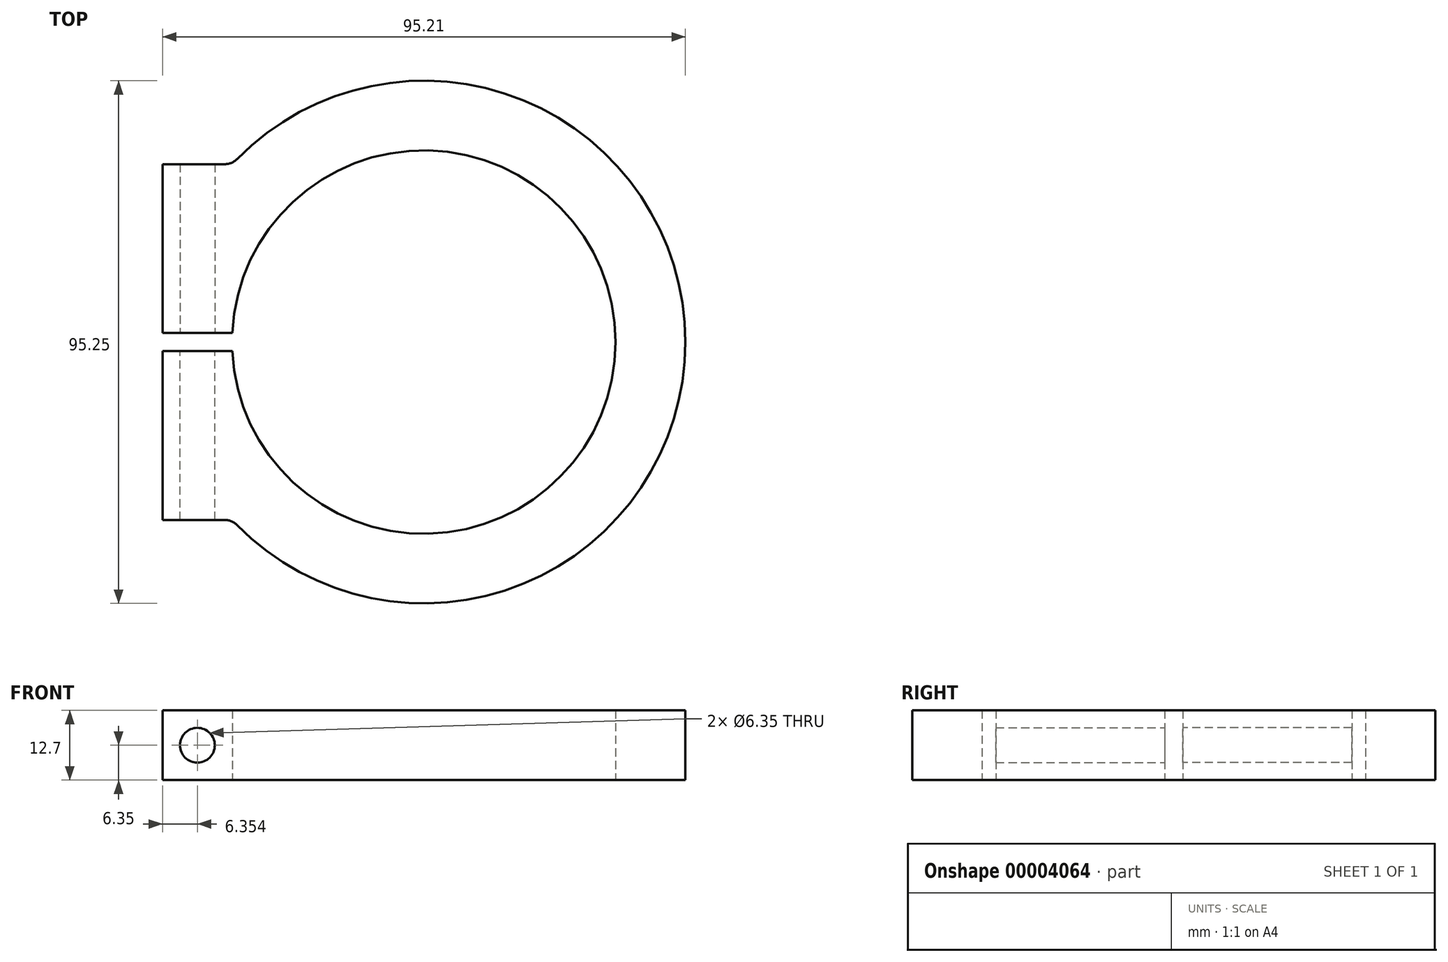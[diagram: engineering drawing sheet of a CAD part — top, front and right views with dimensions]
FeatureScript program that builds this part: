
annotation { "Feature Type Name" : "Feature", "Feature Type Description" : "" }
export const myFeature = defineFeature(function(context is Context, id is Id, definition is map)
    precondition{}
    {
        {
            var Q0;
            Q0=qCreatedBy(makeId("Top.planeOp"),FACE);
            var sketch = newSketch(context, id + "F0", { "sketchPlane" : qUnion([Q0])});
            skArc(sketch, "E0", {"start": v(0, 34.93) * mm, "mid": v(-24.1, 25.27) * mm, "end": v(-34.89, 1.65) * mm});
            skLineSegment(sketch, "E1", {"start": v(-34.89, 1.65) * mm, "end": v(-47.6, 1.65) * mm});
            skLineSegment(sketch, "E2", {"start": v(-47.59, 1.65) * mm, "end": v(-47.59, 8) * mm});
            skLineSegment(sketch, "E3", {"start": v(-47.59, 1.65) * mm, "end": v(-47.6, 1.65) * mm});
            skLineSegment(sketch, "E4", {"start": v(0, 0) * mm, "end": v(0, 34.93) * mm, "construction": true});
            skLineSegment(sketch, "E5", {"start": v(0, 34.93) * mm, "end": v(0, 47.7) * mm, "construction": true});
            skArc(sketch, "E6.0.MirrorCS", {"start": v(0, 34.93) * mm, "mid": v(24.1, 25.27) * mm, "end": v(34.89, 1.65) * mm});
            skArc(sketch, "E7", {"start": v(-34.89, -1.65) * mm, "mid": v(34.93, 0) * mm, "end": v(-34.89, 1.65) * mm});
            skPoint(sketch, "E8.0.MirrorCS.start.orphan", {"position": v(47.6, 1.65) * mm});
            skPoint(sketch, "E9.0.MirrorCS.end.orphan", {"position": v(47.59, 8) * mm});
            skPoint(sketch, "E9.0.MirrorCS.start.orphan", {"position": v(47.59, 1.65) * mm});
            skLineSegment(sketch, "E10", {"start": v(-47.6, -1.65) * mm, "end": v(-47.59, -1.65) * mm});
            skArc(sketch, "E11", {"start": v(-33.98, -33.37) * mm, "mid": v(47.63, 0) * mm, "end": v(-33.98, 33.37) * mm});
            skLineSegment(sketch, "E12", {"start": v(-47.59, -1.65) * mm, "end": v(-47.59, -8) * mm});
            skLineSegment(sketch, "E13", {"start": v(-47.6, -1.65) * mm, "end": v(-34.89, -1.65) * mm});
            skLineSegment(sketch, "E14", {"start": v(-34.89, 1.65) * mm, "end": v(-34.89, 32.42) * mm, "construction": true});
            skLineSegment(sketch, "E15", {"start": v(-34.89, -1.65) * mm, "end": v(-34.89, -32.42) * mm, "construction": true});
            skLineSegment(sketch, "E16", {"start": v(-36.24, 32.42) * mm, "end": v(-44.41, 32.42) * mm});
            skLineSegment(sketch, "E17", {"start": v(-47.59, 19.02) * mm, "end": v(-47.59, 8) * mm});
            skLineSegment(sketch, "E18", {"start": v(-36.24, -32.42) * mm, "end": v(-44.41, -32.42) * mm});
            skLineSegment(sketch, "E19", {"start": v(-47.59, -19.02) * mm, "end": v(-47.59, -8) * mm});
            skPoint(sketch, "E20.orphan", {"position": v(-46.72, 9.22) * mm});
            skPoint(sketch, "E21.visualSharp", {"position": v(-34.89, 32.42) * mm});
            skArc(sketch, "E21.filletArc", {"start": v(-36.24, 32.42) * mm, "mid": v(-35.02, 32.67) * mm, "end": v(-33.98, 33.37) * mm});
            skArc(sketch, "E22", {"start": v(-33.98, 33.37) * mm, "mid": v(-38.5, 37.82) * mm, "end": v(-33.98, 33.37) * mm});
            skArc(sketch, "E23", {"start": v(-33.98, 33.37) * mm, "mid": v(33.98, -33.37) * mm, "end": v(-33.98, 33.37) * mm});
            skPoint(sketch, "E24.0.MirrorCS.end.orphan", {"position": v(46.72, 9.22) * mm});
            skPoint(sketch, "E25.visualSharp", {"position": v(-34.89, -32.42) * mm});
            skArc(sketch, "E25.filletArc", {"start": v(-33.98, -33.37) * mm, "mid": v(-35.02, -32.67) * mm, "end": v(-36.24, -32.42) * mm});
            skPoint(sketch, "E26.visualSharp", {"position": v(-47.59, 32.42) * mm});
            skPoint(sketch, "E27.visualSharp", {"position": v(-47.59, -32.42) * mm});
            skLineSegment(sketch, "E28", {"start": v(-44.41, -32.42) * mm, "end": v(-47.59, -32.42) * mm});
            skLineSegment(sketch, "E29", {"start": v(-47.59, -19.02) * mm, "end": v(-47.59, -32.42) * mm});
            skLineSegment(sketch, "E30", {"start": v(-44.41, 32.42) * mm, "end": v(-47.59, 32.42) * mm});
            skLineSegment(sketch, "E31", {"start": v(-47.59, 32.42) * mm, "end": v(-47.59, 19.02) * mm});
            skSolve(sketch);
        }
        {
            var Q0;
            {var subQ5=sQuery(id+"F0.wireOp",EDGE,"E1");Q0=makeQuery(id+"F0.imprint","IMPRINT",FACE,{"disambiguationData":[TD([[makeQuery(id+"F0.imprint","IMPRINT",EDGE,{"derivedFrom":subQ5}),-1.0]])]});}
            extrude(context, id + "F1", {"entities" : qUnion([Q0]), "depth" : 12.7 * mm});
        }
        {
            var Q0;
            Q0=makeQuery(id+"F1.opExtrude","SWEPT_FACE",FACE,{"disambiguationData":[OSD([sQuery(id+"F0.wireOp",EDGE,"E13")])]});
            var sketch = newSketch(context, id + "F2", { "sketchPlane" : qUnion([Q0])});
            skCircle(sketch, "E32", {"center": v(41.24, 6.35) * mm, "radius": 3.18 * mm});
            skCircle(sketch, "E33", {"center": v(41.24, 6.35) * mm, "radius": 6.35 * mm});
            skSolve(sketch);
        }
        {
            var Q0;
            Q0=makeQuery(id+"F2.imprint","IMPRINT",FACE,{"disambiguationData":[TD([[makeQuery(id+"F2.imprint","IMPRINT",EDGE,{"derivedFrom":sQuery(id+"F2.wireOp",EDGE,"E32")}),1.0]])]});
            extrude(context, id + "F3", {"entities" : qUnion([Q0]), "operationType" : NewBodyOperationType.REMOVE, "endBound" : BoundingType.THROUGH_ALL, "oppositeDirection" : true, "depth" : 25.4 * mm});
        }
        {
            var Q0;
            Q0=makeQuery(id+"F2.imprint","IMPRINT",FACE,{"disambiguationData":[TD([[makeQuery(id+"F2.imprint","IMPRINT",EDGE,{"derivedFrom":sQuery(id+"F2.wireOp",EDGE,"E32")}),1.0]])]});
            extrude(context, id + "F4", {"entities" : qUnion([Q0]), "operationType" : NewBodyOperationType.REMOVE, "endBound" : BoundingType.THROUGH_ALL, "depth" : 25.4 * mm});
        }
    });
